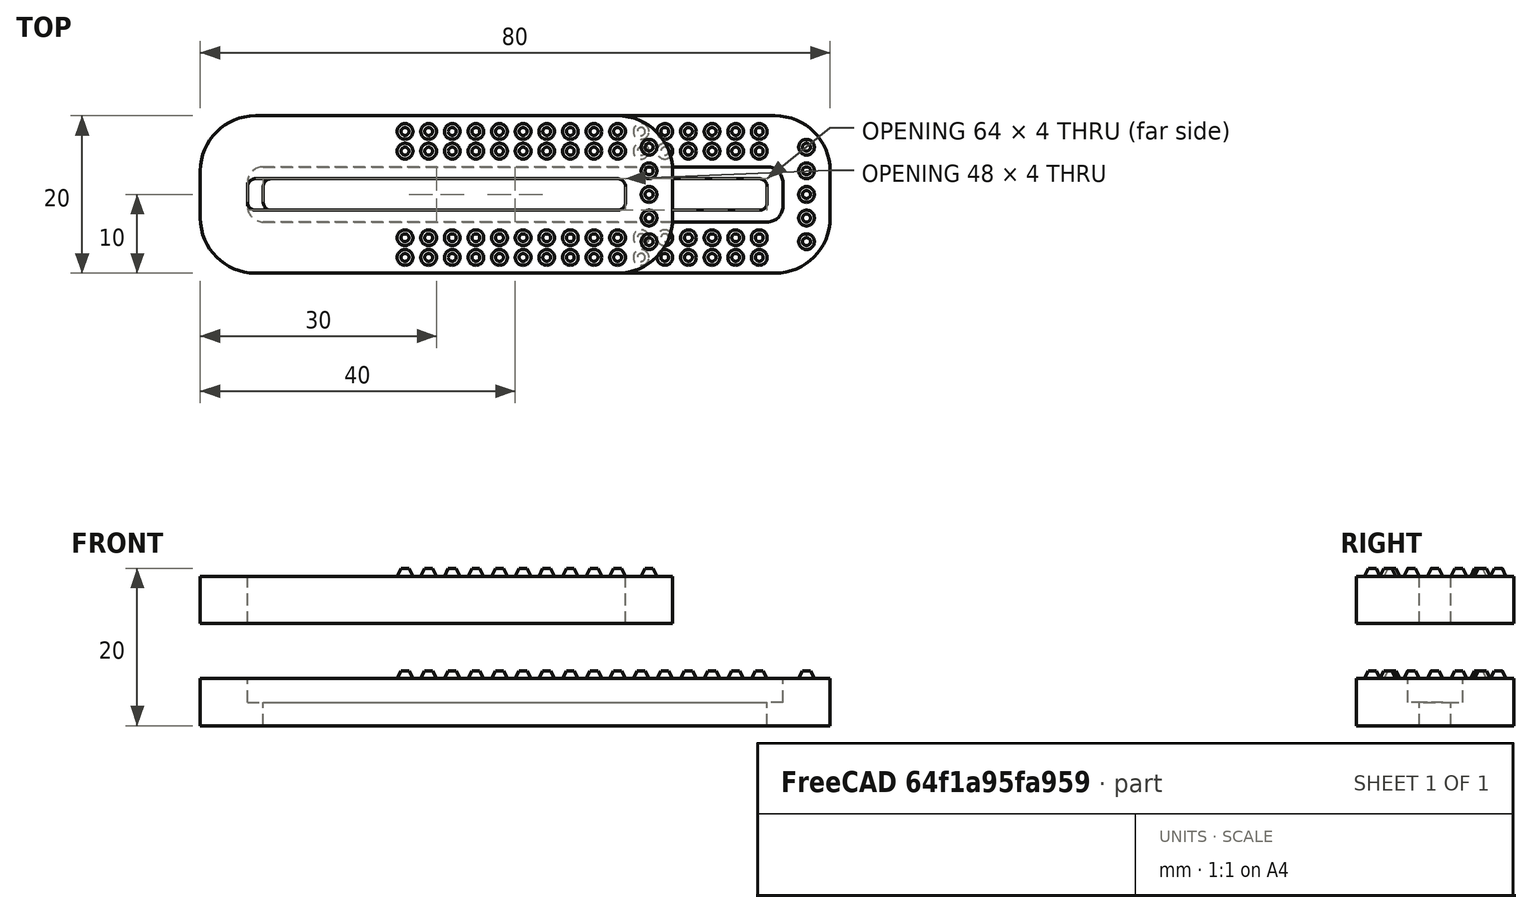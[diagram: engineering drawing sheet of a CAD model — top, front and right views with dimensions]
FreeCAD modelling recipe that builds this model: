
FCSTD DOCUMENT  (FreeCAD 0.19R23578 (Git))
Label: cnc_holder
License: All rights reserved
LicenseURL: http://en.wikipedia.org/wiki/All_rights_reserved
objects: Part::Box×5, Part::Fillet×5, Part::FeaturePython×4, Part::MultiFuse×3, Spreadsheet::Sheet×2, PartDesign::FeatureBase×2, PartDesign::Body×2, Part::Cut×2, PartDesign::AdditiveCone×2, Part::Mirroring×2, App::Part×1
note: 29 computed .brp shape members not serialized (recipe doc carries the construction recipe); baked Part::Feature solids carry a one-line shape summary decoded from their .brp

FEATURE [Part::Box] Box  label="bottom base cube"
  AttacherType = Attacher::AttachEngine3D
  Height = 6
  Length = 80
  Width = 20
  expr: Length = <<p>>.base_length
  expr: Width = <<p>>.base_width
  expr: Height = <<p>>.base_height
FEATURE [Part::Box] Box001  label="bottom extract cube"
  AttacherType = Attacher::AttachEngine3D
  Height = 20
  Length = 64
  Placement = pos=(8,8,0) rot=(0,0,1;0rad)
  Width = 4
  expr: .Placement.Base.y = (<<p>>.base_width - <<p>>.bottom_extract_width) / 2
  expr: .Placement.Base.x = <<p>>.side_pad + <<p>>.bottom_extract_width / 2
  expr: Width = <<p>>.bottom_extract_width
  expr: Length = <<p>>.base_length - 2 * <<p>>.side_pad - <<p>>.bottom_extract_width
FEATURE [Part::Fillet] Fillet  label="bottom extract fillet"
  Base = -> Box001
  Edges = 4 edges r=1: [Edge1,Edge3,Edge5,Edge7]
FEATURE [Spreadsheet::Sheet] Spreadsheet  label="p"
  cells = A1=base_length; B1(base_length)=80; A2=base_width; B2(base_width)=20; A3=base_height; B3(base_height)=6; A4=hole_length; B4(hole_length)=40; A5=hole_width; B5(hole_width)=3.6; A6=top_extract_width; B6(top_extract_width)=7; A7=bottom_extract_width; B7(bottom_extract_width)=4; A8=side_pad; B8(side_pad)=6; A9=bolt_head_height; B9(bolt_head_height)=3; A10=stock_height; B10(stock_height)=7; A11=top_base_length; B11(top_base_length)=60; A12=top_base_dot_count; B12(top_base_dot_count)=10; A13=bottom_base_dot_count; B13(bottom_base_dot_count)=16
FEATURE [Part::Box] Box002  label="top extract cube"
  AttacherType = Attacher::AttachEngine3D
  Height = 20
  Length = 68
  Placement = pos=(6,6.5,3) rot=(0,0,1;0rad)
  Width = 7
  expr: .Placement.Base.y = (<<p>>.base_width - <<p>>.top_extract_width) / 2
  expr: .Placement.Base.x = <<p>>.side_pad
  expr: Width = <<p>>.top_extract_width
  expr: Length = <<p>>.base_length - 2 * <<p>>.side_pad
  expr: .Placement.Base.z = <<p>>.base_height - <<p>>.bolt_head_height
FEATURE [Part::Fillet] Fillet001  label="top extract fillet"
  Base = -> Box002
  Edges = 4 edges r=2: [Edge1,Edge3,Edge5,Edge7]
FEATURE [Part::MultiFuse] Fusion  label="extract fusion"
  Shapes = -> [Fillet,Fillet001]
FEATURE [Part::Box] Box003  label="top base cube"
  AttacherType = Attacher::AttachEngine3D
  Height = 6
  Length = 60
  Placement = pos=(0,0,13) rot=(0,0,1;0rad)
  Width = 20
  expr: Length = <<p>>.top_base_length
  expr: Width = <<p>>.base_width
  expr: Height = <<p>>.base_height
  expr: .Placement.Base.z = <<p>>.base_height + <<p>>.stock_height
FEATURE [PartDesign::FeatureBase] Clone
  BaseFeature = -> Fusion
FEATURE [PartDesign::Body] Body  label="extract fusion clone"
  BaseFeature = -> Fusion
  Group = -> [Clone]
  Origin = -> Origin001
  Tip = -> Clone
FEATURE [Part::Fillet] Fillet002  label="bottom base fillet"
  Base = -> Box
  Edges = 4 edges r=7: [Edge1,Edge3,Edge5,Edge7]
FEATURE [Part::Cut] Cut  label="bottom base cut"
  Base = -> Fillet002
  Tool = -> Body
FEATURE [PartDesign::AdditiveCone] Cone  label="dot cone"
  Angle = 360
  AttacherType = Attacher::AttachEngine3D
  Height = 1
  MapMode = 5
  Placement = pos=(0,0,6) rot=(0,0,1;0rad)
  Radius1 = 1
  Radius2 = 0.5
  Support = -> [Cut]
FEATURE [Part::FeaturePython] Array  label="dot array"  # Draft array (typed FeaturePython)
  Angle = 360
  ArrayType = 0
  Axis = (0,0,1)
  Base = -> Cone
  Center = (0,0,0)
  Fuse = false
  IntervalAxis = (0,0,0)
  IntervalX = (3,0,0)
  IntervalY = (0,2.5,0)
  IntervalZ = (0,0,1)
  NumberPolar = 1
  NumberX = 16
  NumberY = 2
  NumberZ = 1
  Placement = pos=(26,2,0) rot=(0,0,1;0rad)
  expr: NumberX = <<p>>.bottom_base_dot_count
FEATURE [Part::Mirroring] Part__Mirroring  label="dot array (Mirror #1)"
  Base = (0,10,0)
  Normal = (0,1,0)
  Source = -> Array
FEATURE [Part::Fillet] Fillet004  label="bottom base fillet001"
  Base = -> Box003
  Edges = 4 edges r=7: [Edge1,Edge3,Edge5,Edge7]
FEATURE [Part::Box] Box005  label="top extract cube001"
  AttacherType = Attacher::AttachEngine3D
  Height = 20
  Length = 48
  Placement = pos=(6,8,0) rot=(0,0,1;0rad)
  Width = 4
  expr: .Placement.Base.y = (<<p>>.base_width - <<p>>.bottom_extract_width) / 2
  expr: .Placement.Base.x = <<p>>.side_pad
  expr: Width = <<p>>.bottom_extract_width
  expr: Length = <<p>>.top_base_length - 2 * <<p>>.side_pad
FEATURE [Part::Fillet] Fillet005  label="top extract fillet001"
  Base = -> Box005
  Edges = 4 edges r=1: [Edge1,Edge3,Edge5,Edge7]
FEATURE [PartDesign::FeatureBase] Clone001
  BaseFeature = -> Fillet005
FEATURE [PartDesign::Body] Body001  label="extract fusion clone001"
  BaseFeature = -> Fillet005
  Group = -> [Clone001]
  Origin = -> Origin002
  Tip = -> Clone001
FEATURE [Part::Cut] Cut001  label="bottom base cut001"
  Base = -> Fillet004
  Tool = -> Body001
FEATURE [Spreadsheet::Sheet] Spreadsheet001  label="p001"
  cells = A1=base_length; B1(base_length)=80; A2=base_width; B2(base_width)=20; A3=base_height; B3(base_height)=6; A4=hole_length; B4(hole_length)=40; A5=hole_width; B5(hole_width)=3.6; A6=top_extract_width; B6(top_extract_width)=7; A7=bottom_extract_width; B7(bottom_extract_width)=4; A8=side_pad; B8(side_pad)=6; A9=bolt_head_height; B9(bolt_head_height)=3; A10=stock_height; B10(stock_height)=7
FEATURE [PartDesign::AdditiveCone] Cone001  label="dot cone001"
  Angle = 360
  AttacherType = Attacher::AttachEngine3D
  Height = 1
  MapMode = 5
  Placement = pos=(0,0,19) rot=(0,0,1;0rad)
  Radius1 = 1
  Radius2 = 0.5
  Support = -> [Cut001]
FEATURE [Part::FeaturePython] Array001  label="dot array001"  # Draft array (typed FeaturePython)
  Angle = 360
  ArrayType = 0
  Axis = (0,0,1)
  Base = -> Cone001
  Center = (0,0,0)
  Fuse = false
  IntervalAxis = (0,0,0)
  IntervalX = (3,0,0)
  IntervalY = (0,2.5,0)
  IntervalZ = (0,0,1)
  NumberPolar = 1
  NumberX = 10
  NumberY = 2
  NumberZ = 1
  Placement = pos=(26,2,0) rot=(0,0,1;0rad)
  expr: NumberX = <<p>>.top_base_dot_count
FEATURE [Part::Mirroring] Part__Mirroring001  label="dot array (Mirror #1)001"
  Base = (0,10,0)
  Normal = (0,1,0)
  Source = -> Array001
FEATURE [Part::FeaturePython] Array002  label="dot array 2"  # Draft array (typed FeaturePython)
  Angle = 360
  ArrayType = 0
  Axis = (0,0,1)
  Base = -> Cone
  Center = (0,0,0)
  Fuse = false
  IntervalAxis = (0,0,0)
  IntervalX = (1,0,0)
  IntervalY = (0,3,0)
  IntervalZ = (0,0,1)
  NumberPolar = 1
  NumberX = 1
  NumberY = 5
  NumberZ = 1
  Placement = pos=(77,4,0) rot=(0,0,1;0rad)
  expr: .Placement.Base.x = <<p>>.base_length - <<p>>.side_pad / 2
FEATURE [Part::MultiFuse] Fusion001  label="bottom fusion"
  Shapes = -> [Array,Part__Mirroring,Cut,Array002]
FEATURE [App::Part] Part  label="cnc holder part"
  Group = -> [Fusion,Fillet,Body,Fillet002,Fillet001,Box,Box001,Box002,Cut,Part__Mirroring,Cone,Array,Fusion001]
  Origin = -> Origin
FEATURE [Part::FeaturePython] Array003  label="dot array 003"  # Draft array (typed FeaturePython)
  Angle = 360
  ArrayType = 0
  Axis = (0,0,1)
  Base = -> Cone001
  Center = (0,0,0)
  Fuse = false
  IntervalAxis = (0,0,0)
  IntervalX = (1,0,0)
  IntervalY = (0,3,0)
  IntervalZ = (0,0,1)
  NumberPolar = 1
  NumberX = 1
  NumberY = 5
  NumberZ = 1
  Placement = pos=(57,4,0) rot=(0,0,1;0rad)
  expr: .Placement.Base.x = <<p>>.top_base_length - <<p>>.side_pad / 2
FEATURE [Part::MultiFuse] Fusion003  label="top fusion"
  Shapes = -> [Array001,Part__Mirroring001,Cut001,Array003]
